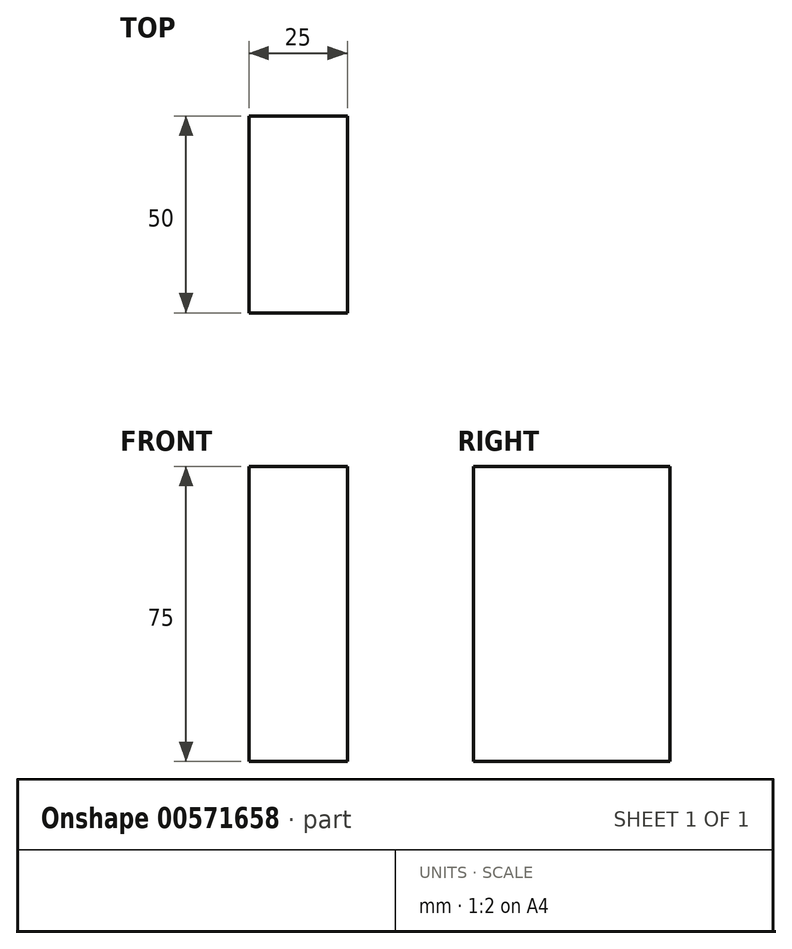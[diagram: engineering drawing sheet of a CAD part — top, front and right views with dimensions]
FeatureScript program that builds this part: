
annotation { "Feature Type Name" : "Feature", "Feature Type Description" : "" }
export const myFeature = defineFeature(function(context is Context, id is Id, definition is map)
    precondition{}
    {
        {
            var Q0;
            Q0=qCreatedBy(makeId("Top.planeOp"),FACE);
            var sketch = newSketch(context, id + "F0", { "sketchPlane" : qUnion([Q0])});
            skLineSegment(sketch, "E0.bottom", {"start": v(0, 0) * mm, "end": v(25, 0) * mm});
            skLineSegment(sketch, "E0.top", {"start": v(0, 50) * mm, "end": v(25, 50) * mm});
            skLineSegment(sketch, "E0.left", {"start": v(0, 0) * mm, "end": v(0, 50) * mm});
            skLineSegment(sketch, "E0.right", {"start": v(25, 0) * mm, "end": v(25, 50) * mm});
            skSolve(sketch);
        }
        {
            var Q0;
            Q0 = qSketchRegion(id + "F0", true);
            extrude(context, id + "F1", {"entities" : qUnion([Q0]), "depth" : 75 * mm, "offsetDistance" : 25 * mm});
        }
    });
